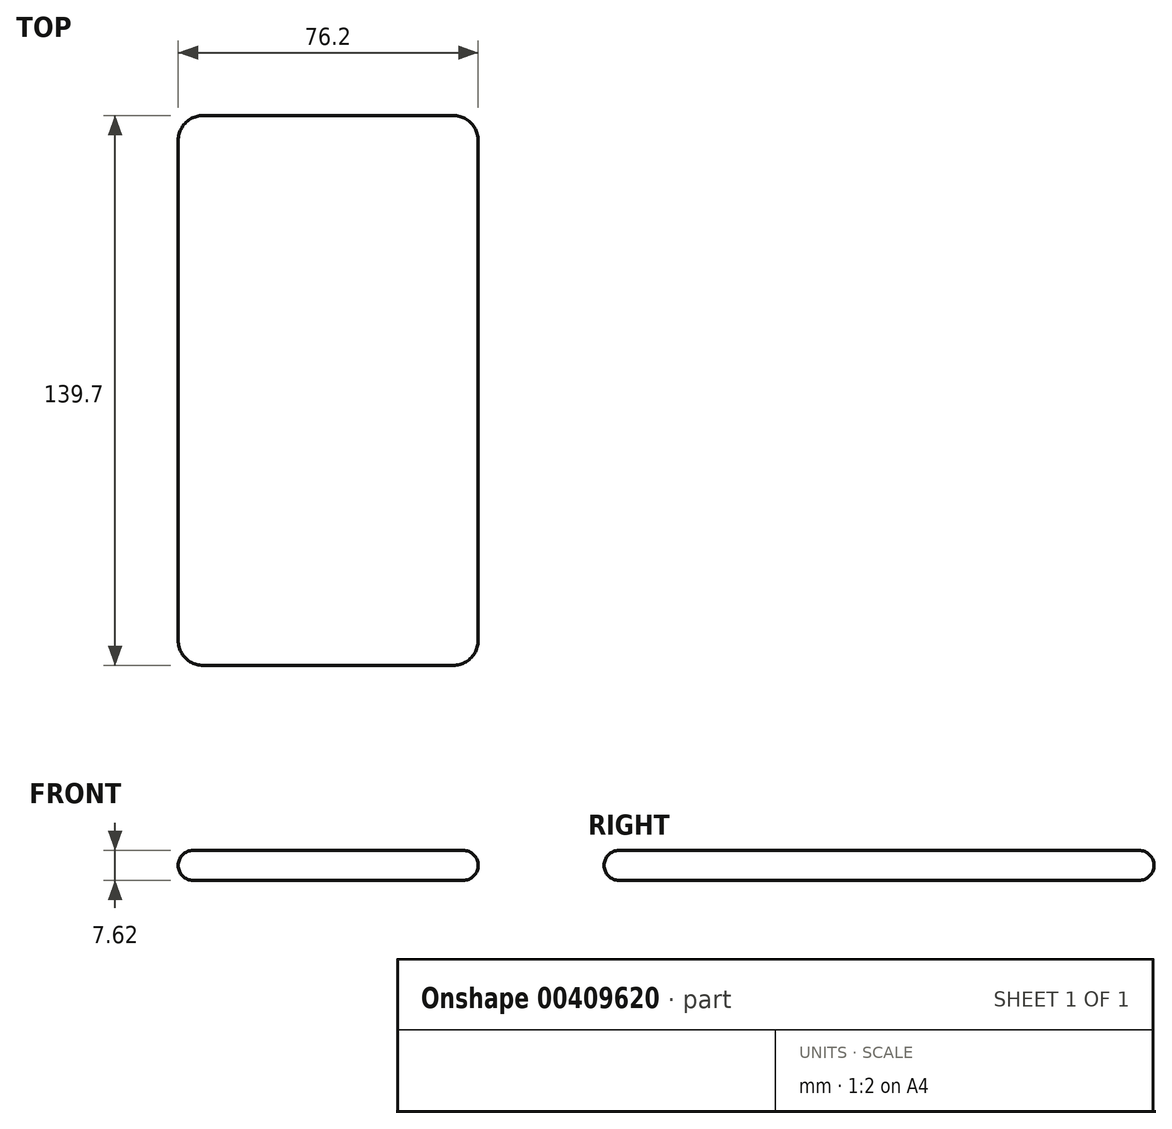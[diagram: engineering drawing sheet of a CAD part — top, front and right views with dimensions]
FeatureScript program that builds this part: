
annotation { "Feature Type Name" : "Feature", "Feature Type Description" : "" }
export const myFeature = defineFeature(function(context is Context, id is Id, definition is map)
    precondition{}
    {
        {
            var Q0;
            Q0=qCreatedBy(makeId("Top.planeOp"),FACE);
            var sketch = newSketch(context, id + "F0", { "sketchPlane" : qUnion([Q0])});
            skLineSegment(sketch, "E0.bottom", {"start": v(6.35, 0) * mm, "end": v(69.85, 0) * mm});
            skLineSegment(sketch, "E0.top", {"start": v(6.35, 139.7) * mm, "end": v(69.85, 139.7) * mm});
            skLineSegment(sketch, "E0.left", {"start": v(0, 6.35) * mm, "end": v(0, 133.35) * mm});
            skLineSegment(sketch, "E0.right", {"start": v(76.2, 6.35) * mm, "end": v(76.2, 133.35) * mm});
            skPoint(sketch, "E1.visualSharp", {"position": v(0, 139.7) * mm});
            skArc(sketch, "E1.filletArc", {"start": v(6.35, 139.7) * mm, "mid": v(1.86, 137.84) * mm, "end": v(0, 133.35) * mm});
            skPoint(sketch, "E2.visualSharp", {"position": v(76.2, 139.7) * mm});
            skArc(sketch, "E2.filletArc", {"start": v(76.2, 133.35) * mm, "mid": v(74.34, 137.84) * mm, "end": v(69.85, 139.7) * mm});
            skPoint(sketch, "E3.visualSharp", {"position": v(76.2, 0) * mm});
            skArc(sketch, "E3.filletArc", {"start": v(69.85, 0) * mm, "mid": v(74.34, 1.86) * mm, "end": v(76.2, 6.35) * mm});
            skPoint(sketch, "E4.visualSharp", {"position": v(0, 0) * mm});
            skArc(sketch, "E4.filletArc", {"start": v(0, 6.35) * mm, "mid": v(1.86, 1.86) * mm, "end": v(6.35, 0) * mm});
            skSolve(sketch);
        }
        {
            var Q0;
            Q0 = qSketchRegion(id + "F0", true);
            extrude(context, id + "F1", {"entities" : qUnion([Q0]), "depth" : 7.62 * mm});
        }
        {
            var Q0;
            Q0=makeQuery(id+"F1.opExtrude","CAP_EDGE",EDGE,{"disambiguationData":[OSD([sQuery(id+"F0.wireOp",EDGE,"E0.left")])],"isStart":false});
            var Q1;
            Q1=makeQuery(id+"F1.opExtrude","CAP_EDGE",EDGE,{"disambiguationData":[OSD([sQuery(id+"F0.wireOp",EDGE,"E0.left")])],"isStart":true});
            fillet(context, id + "F2", {"entities" : qUnion([Q0, Q1]), "radius" : 3.8 * mm, "tangentPropagation" : true, "allowEdgeOverflow" : false});
        }
    });
